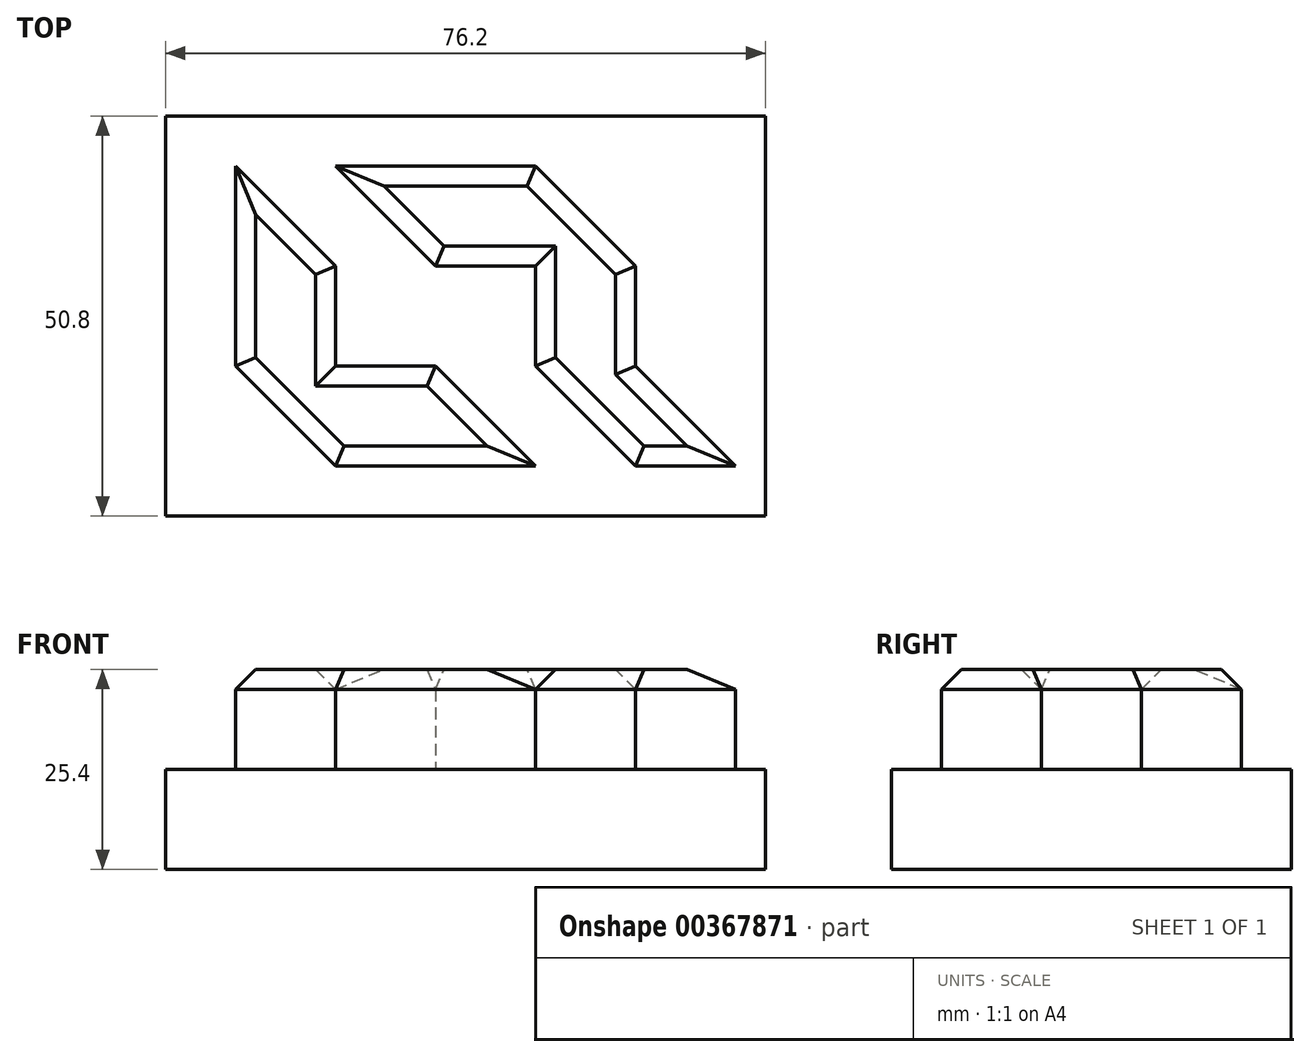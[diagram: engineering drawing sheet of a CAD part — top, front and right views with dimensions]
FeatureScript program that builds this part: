
annotation { "Feature Type Name" : "Feature", "Feature Type Description" : "" }
export const myFeature = defineFeature(function(context is Context, id is Id, definition is map)
    precondition{}
    {
        {
            var Q0;
            Q0=qCreatedBy(makeId("Top.planeOp"),FACE);
            var sketch = newSketch(context, id + "F0", { "sketchPlane" : qUnion([Q0])});
            skLineSegment(sketch, "E0.bottom", {"start": v(0, 0) * mm, "end": v(76.2, 0) * mm});
            skLineSegment(sketch, "E0.top", {"start": v(0, 50.8) * mm, "end": v(76.2, 50.8) * mm});
            skLineSegment(sketch, "E0.left", {"start": v(0, 0) * mm, "end": v(0, 50.8) * mm});
            skLineSegment(sketch, "E0.right", {"start": v(76.2, 0) * mm, "end": v(76.2, 50.8) * mm});
            skSolve(sketch);
        }
        {
            var Q0;
            Q0 = qSketchRegion(id + "F0", true);
            extrude(context, id + "F1", {"entities" : qUnion([Q0]), "depth" : 25.4 * mm});
        }
        {
            var Q0;
            Q0=makeQuery(id+"F1.opExtrude","CAP_FACE",FACE,{"disambiguationData":[OSD([sQuery(id+"F0.wireOp",EDGE,"E0.bottom"),sQuery(id+"F0.wireOp",EDGE,"E0.top"),sQuery(id+"F0.wireOp",EDGE,"E0.left"),sQuery(id+"F0.wireOp",EDGE,"E0.right")])],"isStart":false});
            var sketch = newSketch(context, id + "F2", { "sketchPlane" : qUnion([Q0])});
            skLineSegment(sketch, "E1.bottom", {"start": v(0, 0) * mm, "end": v(76.2, 0) * mm});
            skLineSegment(sketch, "E1.top", {"start": v(0, 50.8) * mm, "end": v(76.2, 50.8) * mm});
            skLineSegment(sketch, "E1.left", {"start": v(0, 0) * mm, "end": v(0, 50.8) * mm});
            skLineSegment(sketch, "E1.right", {"start": v(76.2, 0) * mm, "end": v(76.2, 50.8) * mm});
            skSolve(sketch);
        }
        {
            var Q0;
            Q0 = qSketchRegion(id + "F2", true);
            extrude(context, id + "F3", {"entities" : qUnion([Q0]), "operationType" : NewBodyOperationType.REMOVE, "oppositeDirection" : true, "depth" : 12.7 * mm});
        }
        {
            var Q0;
            Q0=makeQuery(id+"F3.boolean.opBoolean","COPY",FACE,{"derivedFrom":makeQuery(id+"F3.opExtrude","CAP_FACE",FACE,{"disambiguationData":[OSD([sQuery(id+"F2.wireOp",EDGE,"E1.bottom"),sQuery(id+"F2.wireOp",EDGE,"E1.top"),sQuery(id+"F2.wireOp",EDGE,"E1.left"),sQuery(id+"F2.wireOp",EDGE,"E1.right")])],"isStart":false})});
            var sketch = newSketch(context, id + "F4", { "sketchPlane" : qUnion([Q0])});
            skLineSegment(sketch, "E2", {"start": v(8.89, 44.45) * mm, "end": v(8.89, 31.75) * mm});
            skLineSegment(sketch, "E3", {"start": v(8.89, 31.75) * mm, "end": v(8.89, 19.05) * mm});
            skLineSegment(sketch, "E4", {"start": v(8.89, 19.05) * mm, "end": v(21.6, 6.35) * mm});
            skLineSegment(sketch, "E5", {"start": v(21.59, 6.35) * mm, "end": v(34.3, 6.35) * mm});
            skLineSegment(sketch, "E6", {"start": v(34.3, 6.35) * mm, "end": v(47, 6.35) * mm});
            skLineSegment(sketch, "E7", {"start": v(47, 6.35) * mm, "end": v(34.3, 19.05) * mm});
            skLineSegment(sketch, "E8", {"start": v(34.3, 19.05) * mm, "end": v(21.59, 19.05) * mm});
            skLineSegment(sketch, "E9", {"start": v(21.59, 19.05) * mm, "end": v(21.59, 31.75) * mm});
            skLineSegment(sketch, "E10", {"start": v(21.59, 31.75) * mm, "end": v(8.89, 44.45) * mm});
            skLineSegment(sketch, "E11", {"start": v(8.89, 25.4) * mm, "end": v(21.59, 25.4) * mm, "construction": true});
            skLineSegment(sketch, "E12", {"start": v(59.69, 6.35) * mm, "end": v(72.39, 6.35) * mm});
            skLineSegment(sketch, "E13", {"start": v(72.39, 6.35) * mm, "end": v(59.69, 19.05) * mm});
            skLineSegment(sketch, "E14", {"start": v(59.69, 19.05) * mm, "end": v(59.69, 31.75) * mm});
            skLineSegment(sketch, "E15", {"start": v(59.69, 31.75) * mm, "end": v(46.99, 44.45) * mm});
            skLineSegment(sketch, "E16", {"start": v(47, 44.45) * mm, "end": v(34.3, 44.45) * mm});
            skLineSegment(sketch, "E17", {"start": v(34.3, 44.45) * mm, "end": v(21.59, 44.45) * mm});
            skLineSegment(sketch, "E18", {"start": v(21.59, 44.45) * mm, "end": v(34.29, 31.75) * mm});
            skLineSegment(sketch, "E19", {"start": v(34.29, 31.75) * mm, "end": v(47, 31.75) * mm});
            skLineSegment(sketch, "E20", {"start": v(47, 31.75) * mm, "end": v(47, 19.05) * mm});
            skLineSegment(sketch, "E21", {"start": v(46.99, 19.05) * mm, "end": v(59.69, 6.35) * mm});
            skSolve(sketch);
        }
        {
            var Q0;
            Q0 = qSketchRegion(id + "F4", true);
            extrude(context, id + "F5", {"entities" : qUnion([Q0]), "operationType" : NewBodyOperationType.ADD, "depth" : 12.7 * mm});
        }
        {
            var Q0;
            Q0=makeQuery(id+"F5.opExtrude","CAP_EDGE",EDGE,{"disambiguationData":[OSD([sQuery(id+"F4.wireOp",EDGE,"E4")])],"isStart":false});
            var Q1;
            Q1=makeQuery(id+"F5.opExtrude","CAP_EDGE",EDGE,{"disambiguationData":[OSD([sQuery(id+"F4.wireOp",EDGE,"E2"),sQuery(id+"F4.wireOp",EDGE,"E3")])],"isStart":false});
            var Q2;
            Q2=makeQuery(id+"F5.opExtrude","CAP_EDGE",EDGE,{"disambiguationData":[OSD([sQuery(id+"F4.wireOp",EDGE,"E10")])],"isStart":false});
            var Q3;
            Q3=makeQuery(id+"F5.opExtrude","CAP_EDGE",EDGE,{"disambiguationData":[OSD([sQuery(id+"F4.wireOp",EDGE,"E9")])],"isStart":false});
            var Q4;
            Q4=makeQuery(id+"F5.opExtrude","CAP_EDGE",EDGE,{"disambiguationData":[OSD([sQuery(id+"F4.wireOp",EDGE,"E8")])],"isStart":false});
            var Q5;
            Q5=makeQuery(id+"F5.opExtrude","CAP_EDGE",EDGE,{"disambiguationData":[OSD([sQuery(id+"F4.wireOp",EDGE,"E7")])],"isStart":false});
            var Q6;
            Q6=makeQuery(id+"F5.opExtrude","CAP_EDGE",EDGE,{"disambiguationData":[OSD([sQuery(id+"F4.wireOp",EDGE,"E5"),sQuery(id+"F4.wireOp",EDGE,"E6")])],"isStart":false});
            var Q7;
            Q7=makeQuery(id+"F5.opExtrude","CAP_EDGE",EDGE,{"disambiguationData":[OSD([sQuery(id+"F4.wireOp",EDGE,"E21")])],"isStart":false});
            var Q8;
            Q8=makeQuery(id+"F5.opExtrude","CAP_EDGE",EDGE,{"disambiguationData":[OSD([sQuery(id+"F4.wireOp",EDGE,"E13")])],"isStart":false});
            var Q9;
            Q9=makeQuery(id+"F5.opExtrude","CAP_EDGE",EDGE,{"disambiguationData":[OSD([sQuery(id+"F4.wireOp",EDGE,"E12")])],"isStart":false});
            var Q10;
            Q10=makeQuery(id+"F5.opExtrude","CAP_EDGE",EDGE,{"disambiguationData":[OSD([sQuery(id+"F4.wireOp",EDGE,"E20")])],"isStart":false});
            var Q11;
            Q11=makeQuery(id+"F5.opExtrude","CAP_EDGE",EDGE,{"disambiguationData":[OSD([sQuery(id+"F4.wireOp",EDGE,"E15")])],"isStart":false});
            var Q12;
            Q12=makeQuery(id+"F5.opExtrude","CAP_EDGE",EDGE,{"disambiguationData":[OSD([sQuery(id+"F4.wireOp",EDGE,"E18")])],"isStart":false});
            var Q13;
            Q13=makeQuery(id+"F5.opExtrude","CAP_EDGE",EDGE,{"disambiguationData":[OSD([sQuery(id+"F4.wireOp",EDGE,"E16"),sQuery(id+"F4.wireOp",EDGE,"E17")])],"isStart":false});
            var Q14;
            Q14=makeQuery(id+"F5.opExtrude","CAP_EDGE",EDGE,{"disambiguationData":[OSD([sQuery(id+"F4.wireOp",EDGE,"E19")])],"isStart":false});
            var Q15;
            Q15=makeQuery(id+"F5.opExtrude","CAP_EDGE",EDGE,{"disambiguationData":[OSD([sQuery(id+"F4.wireOp",EDGE,"E14")])],"isStart":false});
            chamfer(context, id + "F6", {"entities" : qUnion([Q0, Q1, Q2, Q3, Q4, Q5, Q6, Q7, Q8, Q9, Q10, Q11, Q12, Q13, Q14, Q15]), "width" : 2.54 * mm, "tangentPropagation" : true});
        }
    });
